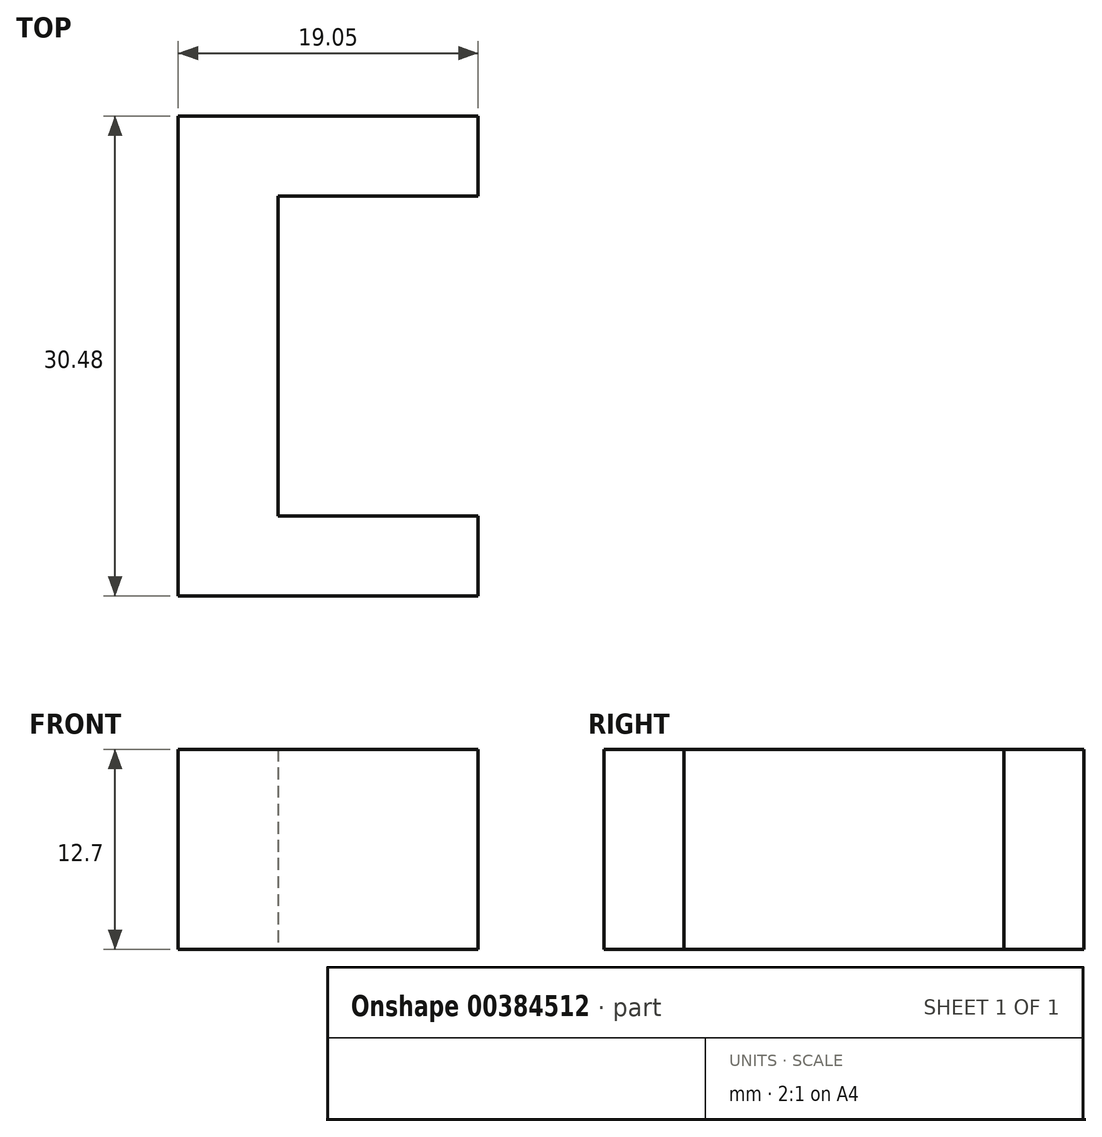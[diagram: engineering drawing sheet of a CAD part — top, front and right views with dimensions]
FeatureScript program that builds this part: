
annotation { "Feature Type Name" : "Feature", "Feature Type Description" : "" }
export const myFeature = defineFeature(function(context is Context, id is Id, definition is map)
    precondition{}
    {
        {
            var Q0;
            Q0=qCreatedBy(makeId("Top.planeOp"),FACE);
            var sketch = newSketch(context, id + "F0", { "sketchPlane" : qUnion([Q0])});
            skLineSegment(sketch, "E0", {"start": v(-37.13, 25.4) * mm, "end": v(-37.13, -5.08) * mm});
            skLineSegment(sketch, "E1", {"start": v(-37.13, 25.4) * mm, "end": v(-18.08, 25.4) * mm});
            skLineSegment(sketch, "E2", {"start": v(-18.08, 25.4) * mm, "end": v(-18.08, 20.32) * mm});
            skLineSegment(sketch, "E3", {"start": v(-18.08, 20.32) * mm, "end": v(-30.78, 20.32) * mm});
            skLineSegment(sketch, "E4", {"start": v(-30.78, 20.32) * mm, "end": v(-30.78, 0) * mm});
            skLineSegment(sketch, "E5", {"start": v(-30.78, 0) * mm, "end": v(-18.08, 0) * mm});
            skLineSegment(sketch, "E6", {"start": v(-18.08, 0) * mm, "end": v(-18.08, -5.08) * mm});
            skLineSegment(sketch, "E7", {"start": v(-18.08, -5.08) * mm, "end": v(-37.13, -5.08) * mm});
            skSolve(sketch);
        }
        {
            var Q0;
            Q0=makeQuery(id+"F0.imprint","IMPRINT",FACE,{"disambiguationData":[TD([[makeQuery(id+"F0.imprint","IMPRINT",EDGE,{"derivedFrom":sQuery(id+"F0.wireOp",EDGE,"E0")}),1.0]])]});
            extrude(context, id + "F1", {"entities" : qUnion([Q0]), "depth" : 12.7 * mm});
        }
    });
